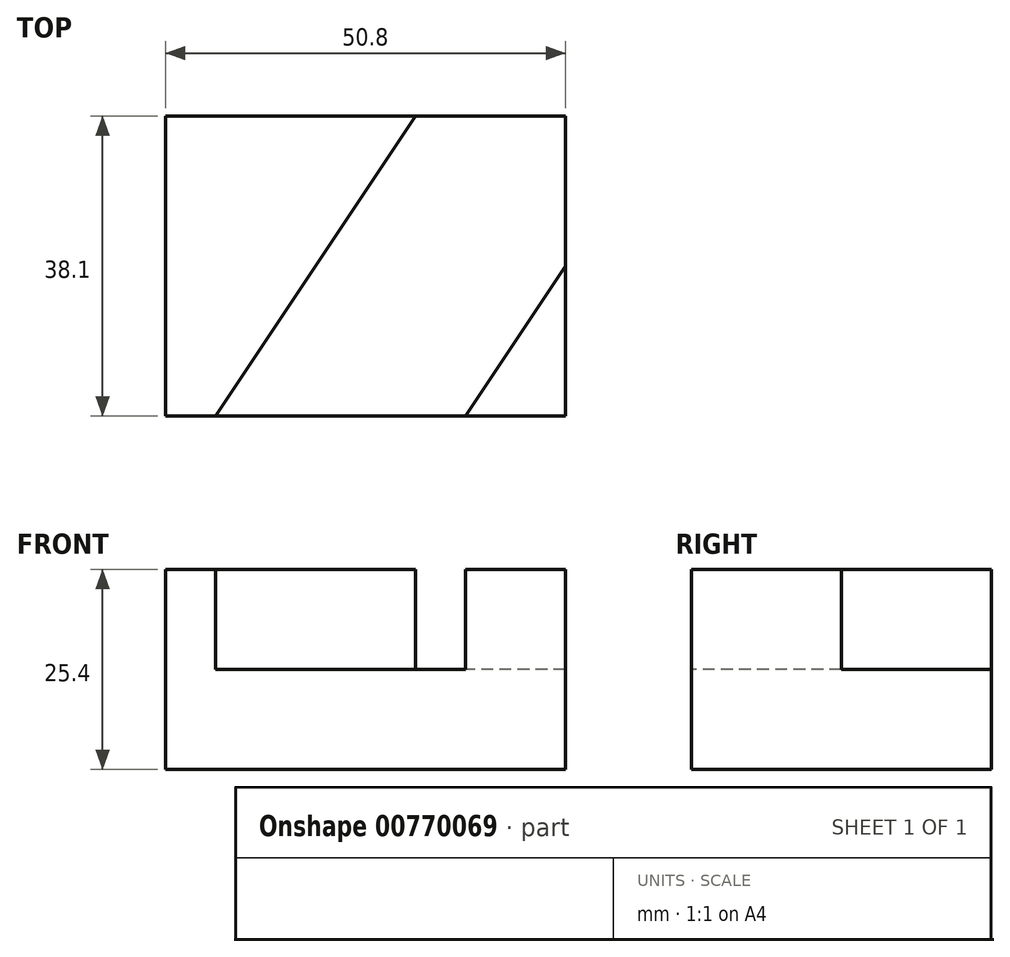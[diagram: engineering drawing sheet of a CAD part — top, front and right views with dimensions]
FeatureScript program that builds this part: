
annotation { "Feature Type Name" : "Feature", "Feature Type Description" : "" }
export const myFeature = defineFeature(function(context is Context, id is Id, definition is map)
    precondition{}
    {
        {
            var Q0;
            Q0=qCreatedBy(makeId("Front.planeOp"),FACE);
            var sketch = newSketch(context, id + "F0", { "sketchPlane" : qUnion([Q0])});
            skLineSegment(sketch, "E0", {"start": v(0, 0) * mm, "end": v(50.8, 0) * mm});
            skLineSegment(sketch, "E1", {"start": v(50.8, 0) * mm, "end": v(50.8, 25.4) * mm});
            skLineSegment(sketch, "E2", {"start": v(50.8, 25.4) * mm, "end": v(0, 25.4) * mm});
            skLineSegment(sketch, "E3", {"start": v(0, 25.4) * mm, "end": v(0, 0) * mm});
            skSolve(sketch);
        }
        {
            var Q0;
            Q0=makeQuery(id+"F0.imprint","IMPRINT",FACE,{"disambiguationData":[TD([[makeQuery(id+"F0.imprint","IMPRINT",EDGE,{"derivedFrom":sQuery(id+"F0.wireOp",EDGE,"E0")}),1.0]])]});
            extrude(context, id + "F1", {"entities" : qUnion([Q0]), "depth" : 38.1 * mm, "offsetDistance" : 25.4 * mm});
        }
        {
            var Q0;
            Q0=makeQuery(id+"F1.opExtrude","SWEPT_FACE",FACE,{"disambiguationData":[OSD([sQuery(id+"F0.wireOp",EDGE,"E2")])]});
            var sketch = newSketch(context, id + "F2", { "sketchPlane" : qUnion([Q0])});
            skLineSegment(sketch, "E4", {"start": v(0, -38.1) * mm, "end": v(6.35, -38.1) * mm});
            skLineSegment(sketch, "E5", {"start": v(0, 0) * mm, "end": v(31.75, 0) * mm});
            skLineSegment(sketch, "E6", {"start": v(31.75, 0) * mm, "end": v(6.35, -38.1) * mm});
            skLineSegment(sketch, "E7", {"start": v(50.8, -38.1) * mm, "end": v(38.1, -38.1) * mm});
            skLineSegment(sketch, "E8", {"start": v(50.8, -38.1) * mm, "end": v(50.8, -19.05) * mm});
            skLineSegment(sketch, "E9", {"start": v(50.8, -19.05) * mm, "end": v(38.1, -38.1) * mm});
            skSolve(sketch);
        }
        {
            var Q0;
            {var subQ4=sQuery(id+"F2.wireOp",EDGE,"E6");Q0=makeQuery(id+"F2.imprint","IMPRINT",FACE,{"disambiguationData":[TD([[makeQuery(id+"F2.imprint","IMPRINT",EDGE,{"derivedFrom":subQ4}),1.0]])]});}
            extrude(context, id + "F3", {"entities" : qUnion([Q0]), "operationType" : NewBodyOperationType.REMOVE, "oppositeDirection" : true, "depth" : 12.7 * mm, "offsetDistance" : 25.4 * mm});
        }
    });
